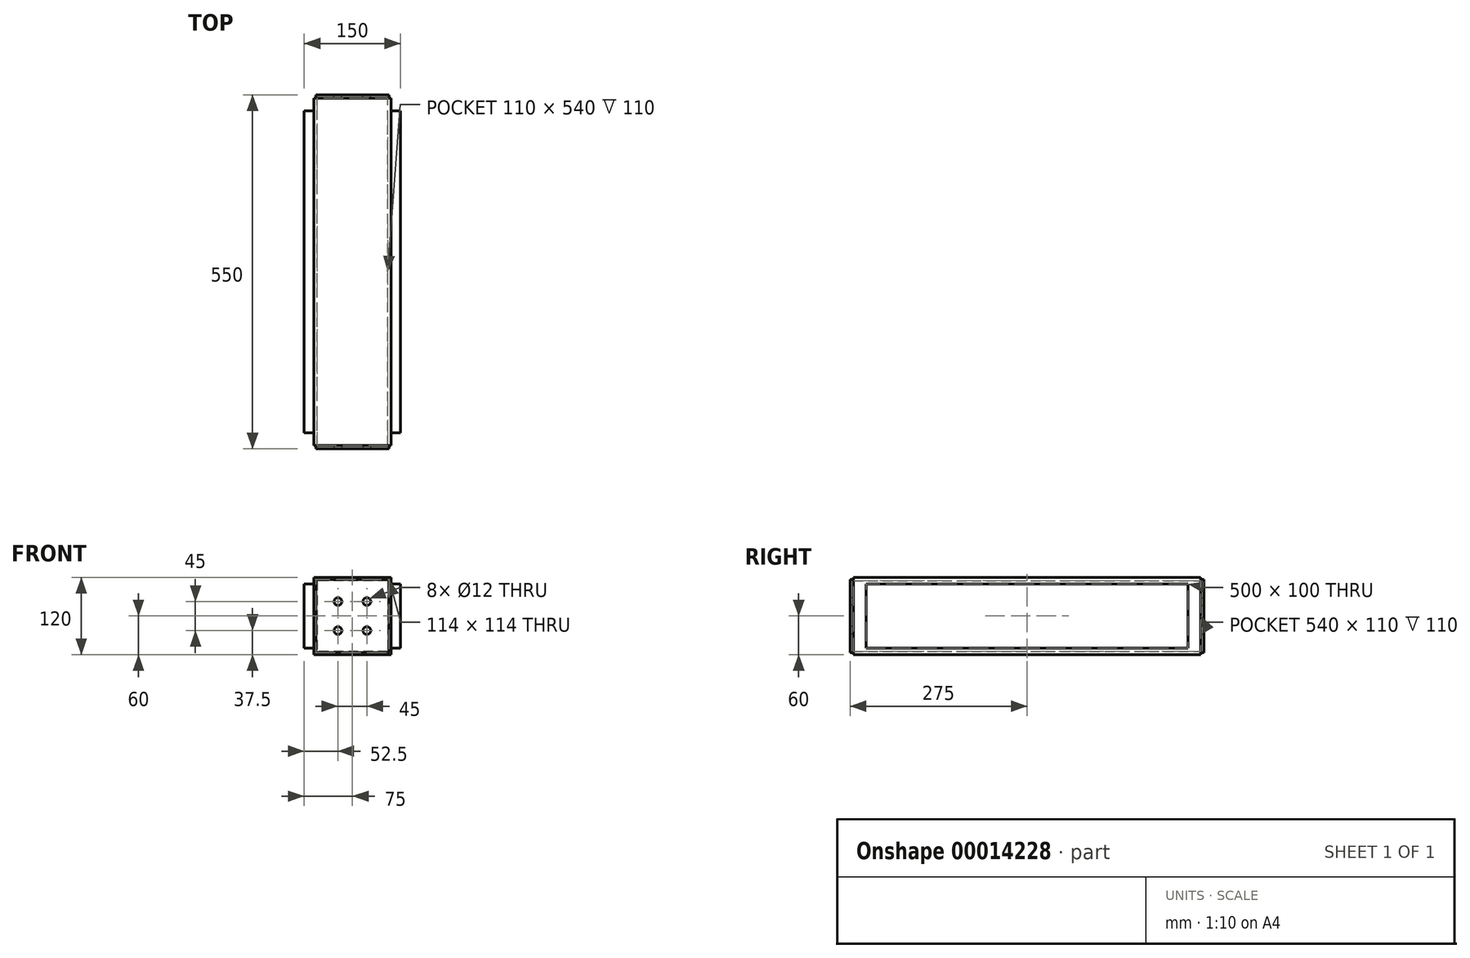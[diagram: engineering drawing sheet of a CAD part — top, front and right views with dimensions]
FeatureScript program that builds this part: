
annotation { "Feature Type Name" : "Feature", "Feature Type Description" : "" }
export const myFeature = defineFeature(function(context is Context, id is Id, definition is map)
    precondition{}
    {
        {
            var Q0;
            Q0=qCreatedBy(makeId("Front.planeOp"),FACE);
            var sketch = newSketch(context, id + "F0", { "sketchPlane" : qUnion([Q0])});
            skLineSegment(sketch, "E0", {"start": v(-72.5, 0) * mm, "end": v(1527.5, 0) * mm, "construction": true});
            skLineSegment(sketch, "E1.rect.bottom", {"start": v(22.5, -22.5) * mm, "end": v(-22.5, -22.5) * mm, "construction": true});
            skLineSegment(sketch, "E1.rect.top", {"start": v(22.5, 22.5) * mm, "end": v(-22.5, 22.5) * mm, "construction": true});
            skLineSegment(sketch, "E1.rect.left", {"start": v(22.5, -22.5) * mm, "end": v(22.5, 22.5) * mm, "construction": true});
            skLineSegment(sketch, "E1.rect.right", {"start": v(-22.5, -22.5) * mm, "end": v(-22.5, 22.5) * mm, "construction": true});
            skPoint(sketch, "E1.rect.middle", {"position": v(0, 0) * mm});
            skCircle(sketch, "E2", {"center": v(-22.5, 22.5) * mm, "radius": 6 * mm});
            skCircle(sketch, "E3", {"center": v(22.5, 22.5) * mm, "radius": 6 * mm});
            skCircle(sketch, "E4", {"center": v(-22.5, -22.5) * mm, "radius": 6 * mm});
            skCircle(sketch, "E5", {"center": v(22.5, -22.5) * mm, "radius": 6 * mm});
            skLineSegment(sketch, "E6.rect.bottom", {"start": v(-57, 57) * mm, "end": v(57, 57) * mm});
            skLineSegment(sketch, "E6.rect.top", {"start": v(-57, -57) * mm, "end": v(57, -57) * mm});
            skLineSegment(sketch, "E6.rect.left", {"start": v(-57, 57) * mm, "end": v(-57, -57) * mm});
            skLineSegment(sketch, "E6.rect.right", {"start": v(57, 57) * mm, "end": v(57, -57) * mm});
            skSolve(sketch);
        }
        {
            var Q0;
            Q0=qSketchRegion(id+"F0",true);
            var Q1;
            Q1=makeQuery(id+"F0.imprint","IMPRINT",FACE,{"disambiguationData":[TD([[makeQuery(id+"F0.imprint","IMPRINT",EDGE,{"derivedFrom":sQuery(id+"F0.wireOp",EDGE,"E3")}),1.0]])]});
            var Q2;
            Q2=makeQuery(id+"F0.imprint","IMPRINT",FACE,{"disambiguationData":[TD([[makeQuery(id+"F0.imprint","IMPRINT",EDGE,{"derivedFrom":sQuery(id+"F0.wireOp",EDGE,"E2")}),1.0]])]});
            var Q3;
            Q3=makeQuery(id+"F0.imprint","IMPRINT",FACE,{"disambiguationData":[TD([[makeQuery(id+"F0.imprint","IMPRINT",EDGE,{"derivedFrom":sQuery(id+"F0.wireOp",EDGE,"E5")}),1.0]])]});
            var Q4;
            Q4=makeQuery(id+"F0.imprint","IMPRINT",FACE,{"disambiguationData":[TD([[makeQuery(id+"F0.imprint","IMPRINT",EDGE,{"derivedFrom":sQuery(id+"F0.wireOp",EDGE,"E4")}),1.0]])]});
            extrude(context, id + "F1", {"entities" : qUnion([Q0, Q1, Q2, Q3, Q4]), "depth" : 5 * mm});
        }
        {
            var Q0;
            Q0=makeQuery(id+"F0.imprint","IMPRINT",FACE,{"disambiguationData":[TD([[makeQuery(id+"F0.imprint","IMPRINT",EDGE,{"derivedFrom":sQuery(id+"F0.wireOp",EDGE,"E5")}),1.0]])]});
            var Q1;
            Q1=makeQuery(id+"F0.imprint","IMPRINT",FACE,{"disambiguationData":[TD([[makeQuery(id+"F0.imprint","IMPRINT",EDGE,{"derivedFrom":sQuery(id+"F0.wireOp",EDGE,"E3")}),1.0]])]});
            var Q2;
            Q2=makeQuery(id+"F0.imprint","IMPRINT",FACE,{"disambiguationData":[TD([[makeQuery(id+"F0.imprint","IMPRINT",EDGE,{"derivedFrom":sQuery(id+"F0.wireOp",EDGE,"E4")}),1.0]])]});
            var Q3;
            Q3=makeQuery(id+"F0.imprint","IMPRINT",FACE,{"disambiguationData":[TD([[makeQuery(id+"F0.imprint","IMPRINT",EDGE,{"derivedFrom":sQuery(id+"F0.wireOp",EDGE,"E2")}),1.0]])]});
            extrude(context, id + "F2", {"entities" : qUnion([Q0, Q1, Q2, Q3]), "operationType" : NewBodyOperationType.REMOVE, "depth" : 15 * mm});
        }
        {
            var Q0;
            Q0=makeQuery(id+"F1.opExtrude","CAP_FACE",FACE,{"disambiguationData":[OSD([sQuery(id+"F0.wireOp",EDGE,"E6.rect.bottom"),sQuery(id+"F0.wireOp",EDGE,"E6.rect.top"),sQuery(id+"F0.wireOp",EDGE,"E6.rect.left"),sQuery(id+"F0.wireOp",EDGE,"E6.rect.right")])],"isStart":false});
            var sketch = newSketch(context, id + "F3", { "sketchPlane" : qUnion([Q0])});
            skLineSegment(sketch, "E7.rect.bottom", {"start": v(60, 60) * mm, "end": v(-60, 60) * mm});
            skLineSegment(sketch, "E7.rect.top", {"start": v(60, -60) * mm, "end": v(-60, -60) * mm});
            skLineSegment(sketch, "E7.rect.left", {"start": v(60, 60) * mm, "end": v(60, -60) * mm});
            skLineSegment(sketch, "E7.rect.right", {"start": v(-60, 60) * mm, "end": v(-60, -60) * mm});
            skPoint(sketch, "E7.rect.middle", {"position": v(0, 0) * mm});
            skLineSegment(sketch, "E8.rect.bottom", {"start": v(55, 55) * mm, "end": v(-55, 55) * mm});
            skLineSegment(sketch, "E8.rect.top", {"start": v(55, -55) * mm, "end": v(-55, -55) * mm});
            skLineSegment(sketch, "E8.rect.left", {"start": v(55, 55) * mm, "end": v(55, -55) * mm});
            skLineSegment(sketch, "E8.rect.right", {"start": v(-55, 55) * mm, "end": v(-55, -55) * mm});
            skSolve(sketch);
        }
        {
            var Q0;
            Q0=qSketchRegion(id+"F3",true);
            extrude(context, id + "F4", {"entities" : qUnion([Q0]), "depth" : 540 * mm});
        }
        {
            var Q0;
            Q0=makeQuery(id+"F4.opExtrude","CAP_FACE",FACE,{"disambiguationData":[OSD([sQuery(id+"F3.wireOp",EDGE,"E7.rect.bottom"),sQuery(id+"F3.wireOp",EDGE,"E7.rect.top"),sQuery(id+"F3.wireOp",EDGE,"E7.rect.left"),sQuery(id+"F3.wireOp",EDGE,"E7.rect.right"),sQuery(id+"F3.wireOp",EDGE,"E8.rect.bottom"),sQuery(id+"F3.wireOp",EDGE,"E8.rect.top"),sQuery(id+"F3.wireOp",EDGE,"E8.rect.left"),sQuery(id+"F3.wireOp",EDGE,"E8.rect.right")])],"isStart":false});
            var sketch = newSketch(context, id + "F5", { "sketchPlane" : qUnion([Q0])});
            skLineSegment(sketch, "E9.rect.bottom", {"start": v(-57, 57) * mm, "end": v(57, 57) * mm});
            skLineSegment(sketch, "E9.rect.top", {"start": v(-57, -57) * mm, "end": v(57, -57) * mm});
            skLineSegment(sketch, "E9.rect.left", {"start": v(-57, 57) * mm, "end": v(-57, -57) * mm});
            skLineSegment(sketch, "E9.rect.right", {"start": v(57, 57) * mm, "end": v(57, -57) * mm});
            skPoint(sketch, "E9.rect.middle", {"position": v(0, 0) * mm});
            skSolve(sketch);
        }
        {
            var Q0;
            Q0=qSketchRegion(id+"F5",true);
            extrude(context, id + "F6", {"entities" : qUnion([Q0]), "depth" : 5 * mm});
        }
        {
            var Q0;
            Q0=makeQuery(id+"F6.opExtrude","CAP_FACE",FACE,{"disambiguationData":[OSD([sQuery(id+"F5.wireOp",EDGE,"E9.rect.bottom"),sQuery(id+"F5.wireOp",EDGE,"E9.rect.top"),sQuery(id+"F5.wireOp",EDGE,"E9.rect.left"),sQuery(id+"F5.wireOp",EDGE,"E9.rect.right")])],"isStart":false});
            var sketch = newSketch(context, id + "F7", { "sketchPlane" : qUnion([Q0])});
            skPoint(sketch, "E10.rect.middle", {"position": v(0, 0) * mm});
            skCircle(sketch, "E11", {"center": v(22.5, 22.5) * mm, "radius": 6 * mm});
            skCircle(sketch, "E12", {"center": v(-22.5, 22.5) * mm, "radius": 6 * mm});
            skCircle(sketch, "E13", {"center": v(22.5, -22.5) * mm, "radius": 6 * mm});
            skCircle(sketch, "E14", {"center": v(-22.5, -22.5) * mm, "radius": 6 * mm});
            skSolve(sketch);
        }
        {
            var Q0;
            Q0=qSketchRegion(id+"F7",true);
            extrude(context, id + "F8", {"entities" : qUnion([Q0]), "operationType" : NewBodyOperationType.REMOVE, "oppositeDirection" : true, "depth" : 15 * mm});
        }
        {
            var Q0;
            Q0=makeQuery(id+"F4.opExtrude","SWEPT_FACE",FACE,{"disambiguationData":[OSD([sQuery(id+"F3.wireOp",EDGE,"E7.rect.left")])]});
            var sketch = newSketch(context, id + "F9", { "sketchPlane" : qUnion([Q0])});
            skLineSegment(sketch, "E15.bottom", {"start": v(-525, 50) * mm, "end": v(-25, 50) * mm});
            skLineSegment(sketch, "E15.top", {"start": v(-525, -50) * mm, "end": v(-25, -50) * mm});
            skLineSegment(sketch, "E15.left", {"start": v(-525, 50) * mm, "end": v(-525, -50) * mm});
            skLineSegment(sketch, "E15.right", {"start": v(-25, 50) * mm, "end": v(-25, -50) * mm});
            skSolve(sketch);
        }
        {
            var Q0;
            Q0=qSketchRegion(id+"F9",true);
            extrude(context, id + "F10", {"entities" : qUnion([Q0]), "operationType" : NewBodyOperationType.ADD, "depth" : 15 * mm});
        }
        {
            var Q0;
            Q0=makeQuery(id+"F4.opExtrude","SWEPT_BODY",BODY,{"disambiguationData":[OSD([sQuery(id+"F3.wireOp",EDGE,"E7.rect.bottom"),sQuery(id+"F3.wireOp",EDGE,"E7.rect.top"),sQuery(id+"F3.wireOp",EDGE,"E7.rect.left"),sQuery(id+"F3.wireOp",EDGE,"E7.rect.right"),sQuery(id+"F3.wireOp",EDGE,"E8.rect.bottom"),sQuery(id+"F3.wireOp",EDGE,"E8.rect.top"),sQuery(id+"F3.wireOp",EDGE,"E8.rect.left"),sQuery(id+"F3.wireOp",EDGE,"E8.rect.right")])]});
            var Q1;
            Q1=qCreatedBy(makeId("Right.planeOp"),FACE);
            mirror(context, id + "F11", {"operationType" : NewBodyOperationType.ADD, "entities" : qUnion([Q0]), "mirrorPlane" : qUnion([Q1])});
        }
    });
